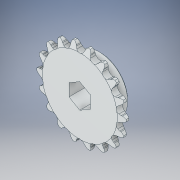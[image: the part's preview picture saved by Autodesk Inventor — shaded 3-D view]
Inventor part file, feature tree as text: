
AUTODESK INVENTOR PART (.ipt)
format: ipt  version: 2019 (Build 230136000, 136)  size: 543,232 bytes
history: native  units: in
note: dims shown in document units (in); Inventor stores cm internally (conversion verified against a paired STEP export)
features: chamfer x1
ambient origin geometry x8: Origin, YZ Plane, XZ Plane, XY Plane, X Axis, Y Axis, Z Axis, Center Point
bodies: Solid1 (feature_tree)
feature tree (1):
  chamfer  "Chamfer2"  [1 undecoded]
note: 1 required parameter value undecoded (feature->parameter linkage not recoverable at this tier; creation-order binding heuristic only, values carry confidence <= 0.55)
